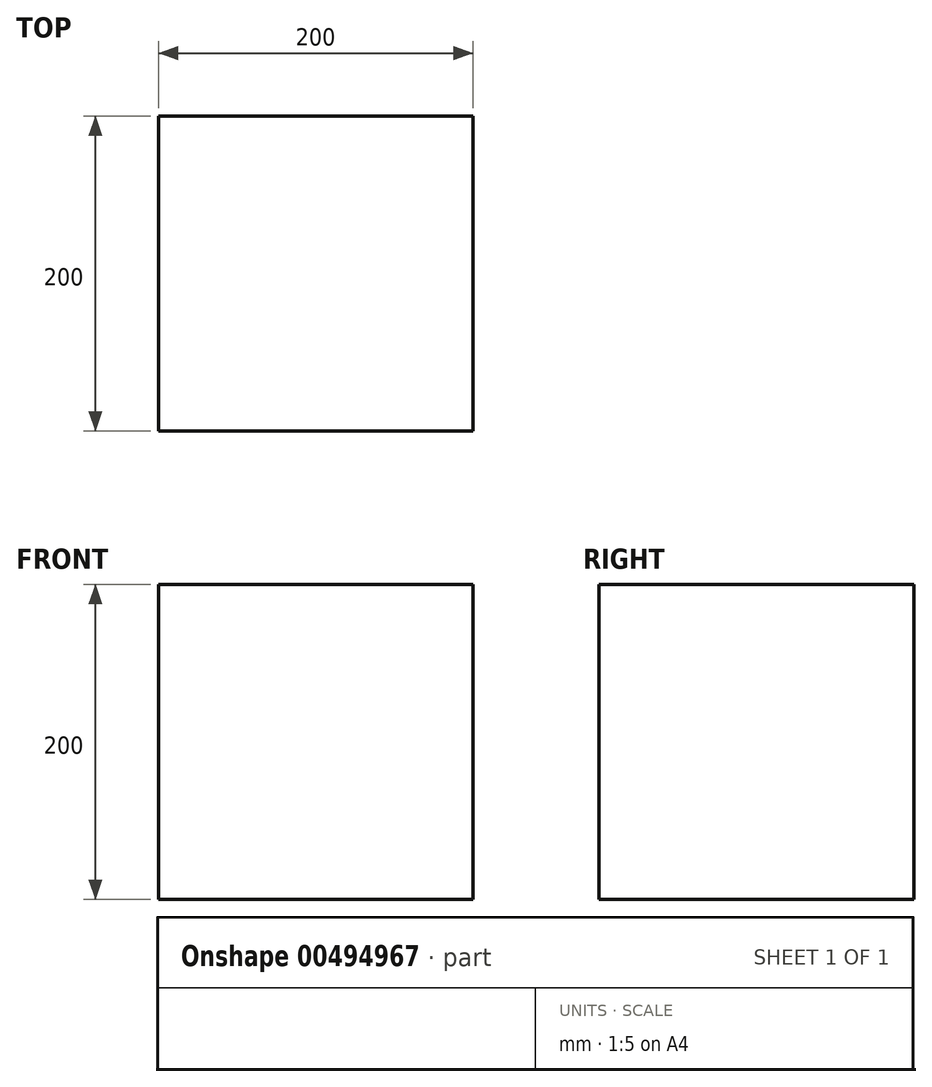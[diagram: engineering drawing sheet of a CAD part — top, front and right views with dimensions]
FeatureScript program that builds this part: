
annotation { "Feature Type Name" : "Feature", "Feature Type Description" : "" }
export const myFeature = defineFeature(function(context is Context, id is Id, definition is map)
    precondition{}
    {
        {
            var Q0;
            Q0=qCreatedBy(makeId("Top.planeOp"),FACE);
            var sketch = newSketch(context, id + "F0", { "sketchPlane" : qUnion([Q0])});
            skLineSegment(sketch, "E0.bottom", {"start": v(-200, 200) * mm, "end": v(0, 200) * mm});
            skLineSegment(sketch, "E0.top", {"start": v(-200, 0) * mm, "end": v(0, 0) * mm});
            skLineSegment(sketch, "E0.left", {"start": v(-200, 200) * mm, "end": v(-200, 0) * mm});
            skLineSegment(sketch, "E0.right", {"start": v(0, 200) * mm, "end": v(0, 0) * mm});
            skSolve(sketch);
        }
        {
            var Q0;
            Q0=qSketchRegion(id+"F0",true);
            extrude(context, id + "F1", {"entities" : qUnion([Q0]), "depth" : 200 * mm});
        }
    });
